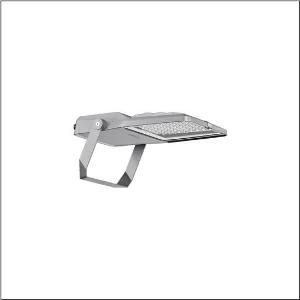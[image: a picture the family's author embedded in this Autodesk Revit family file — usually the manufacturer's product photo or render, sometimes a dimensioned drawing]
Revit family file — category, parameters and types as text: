
# Revit family: floodlight_fl_21_iq_mini___pl64_5xa7772b4e1a_46a5
name_source: partatom
category: Lighting Fixtures
units: mm (PartAtom-declared; Revit-internal decimal feet)

## family parameters
Cut with Voids When Loaded = No
Host = Face
Light Source = No
Part Type = Normal
Room Calculation Point = No
Round Connector Dimension = Use Diameter
Shared = No

## types (1)
- --- (1 x LED, 6270 lm, 45.5 W, 4000K)
    Apparent Load = 46 VA
    CIE Flux Codes = 28 80 98 100 100
    Color Rendering = 70
    Color Temperature = 4000K
    Default Elevation = 1800 mm
    Description = Floodlight FL 21 iQ mini, floodlight, primary light control with lens, of PMMA, primary optical cover: protective disc, of toughened safety glass, transparent, light distribution: PL64, light emission: direct distribution, installation type: surface-mounted, LED, High Power LED, rated luminous flux: 6.270lm, luminous efficacy: 138lm/W, light colour: 740, colour temperature: 4000K, control: Street-Remote, Auto-Match, Temp-Guard, Night-Set, Smart-Wire, Desk-Remote (wireless, voltage-free reading and setting of iQ features in the workshop via application-optimized NFC function/RFID function), optimised constant luminous flux control (CLO 2.0), with terminal, 6-pole, mains connection: 220..240V, AC, 50/60Hz, start of lifetime: 46W, end of service life: 48W, reduction: 22W, luminaire housing, of diecast aluminium, powder-coated, Siteco® metallic grey (DB 702S), corrosivity category C5 mid according to DIN EN ISO 12944, sealing non-destructively replaceable, mounting bracket, of steel, galvanised, powder-coated, Siteco® metallic grey (DB 702S), protection rating (complete): IP66, insulation class (complete): insulation class II (safety insulation), certification: CE, ENEC, VDE, protection symbol: D, impact resistance: IK08, permissible operating ambient temperature: -40..+40°C, permissible operating ambient temperature for outdoor applications: -40..+50°C, standard: DIN EN 12944, LABS conformity tested according to VDMA 24364:2018-05, packaging unit: 1 piece

Light Distribution: PL64
    Height = 70 mm
    Lamp = 1 x LED
    Lamp Light Flux = 6270 lm
    Lamp Power = 45.5 W
    Lamp count = 1
    Length = 485 mm
    Luminous efficacy = 138 lm/W
    Manufacturer = Siteco
    ModVariant = No
    Model = 5XA7772B4E1A
    Number of Poles = 1
    OnlyDefault = Yes
    Power Factor = 1
    Product Name = Floodlight FL 21 iQ mini | PL64
    Product group = floodlight | pylon annexe
    ProductGroupID = 6200
    Protection Class = Protection class II
    Protection Degree = IP 66
    RLX_Detail_Level = 1
    RLX_Emergency_Light_Flux = 0 lm
    RLX_Emergency_Type = 0
    RLX_Emergency_Type_DB = No
    RlxData = <blob elided: 96181 chars, md5=e2321902>
    Socket = socket
    Standby Power = 0 W
    System Light Flux = 6270 lm
    System Power = 46 W
    Type Comments = factory setting: luminous flux: 100 % | dim-lin: 254 | 463 mA
    Type Image = l_1006845.jpg
    URL = http://relux.com
    VarID = @adj_099129
    Voltage = 0 V
    Weight = 0.00 kg
    Width = 337 mm

## geometry (parser evidence)
native form markers: Blend x4, Sweep x14
no freeform markers — native parametric forms only
